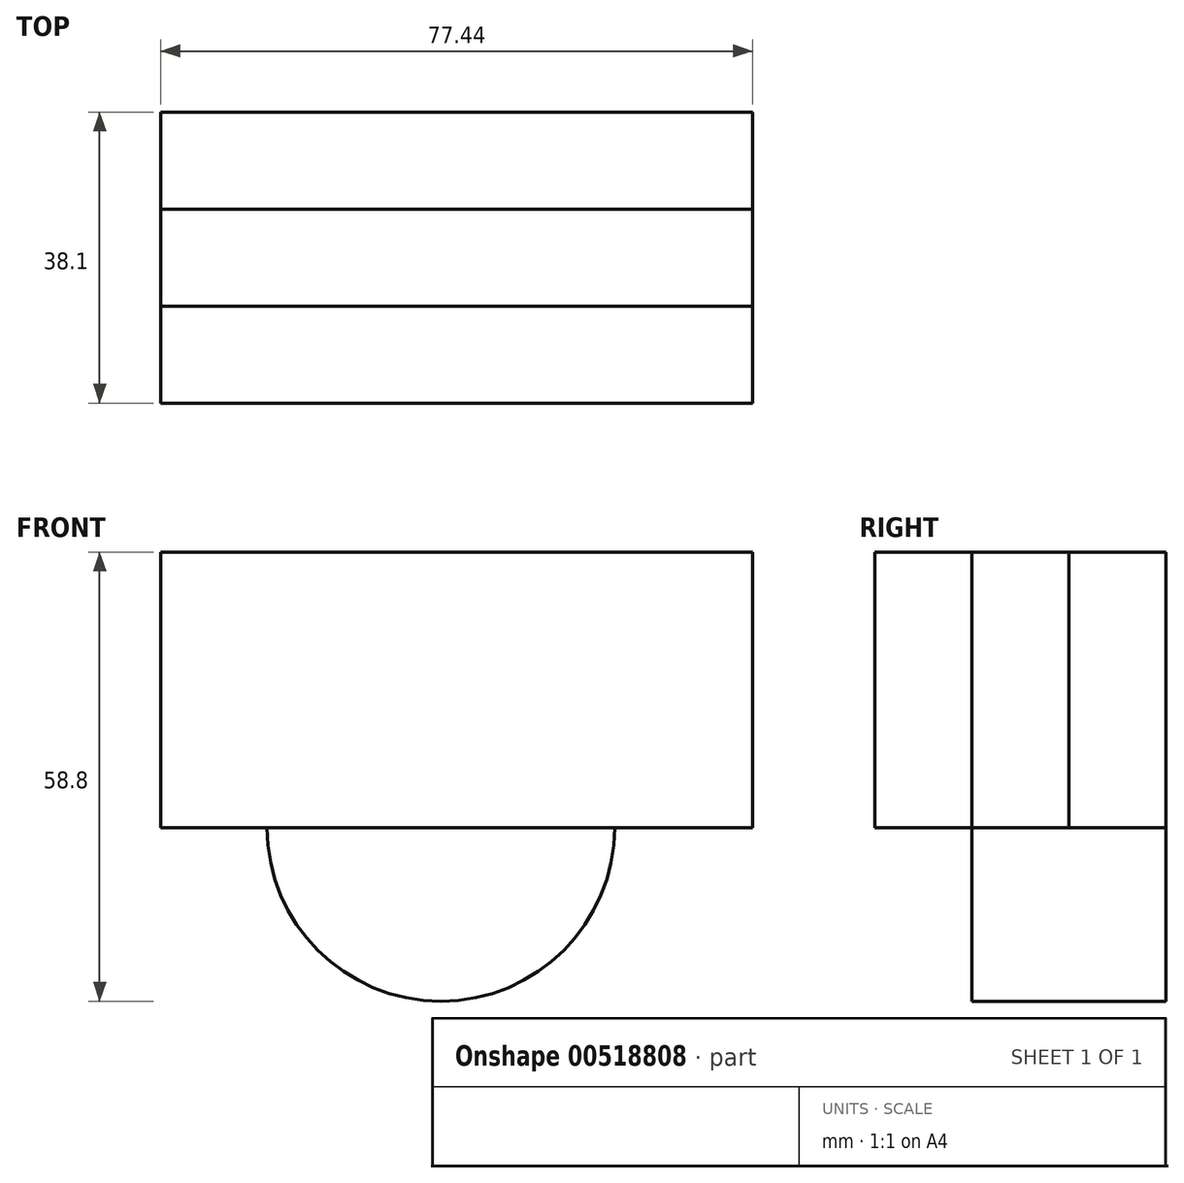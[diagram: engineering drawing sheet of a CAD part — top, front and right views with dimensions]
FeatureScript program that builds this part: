
annotation { "Feature Type Name" : "Feature", "Feature Type Description" : "" }
export const myFeature = defineFeature(function(context is Context, id is Id, definition is map)
    precondition{}
    {
        {
            var Q0;
            Q0=qCreatedBy(makeId("Front.planeOp"),FACE);
            var sketch = newSketch(context, id + "F0", { "sketchPlane" : qUnion([Q0])});
            skLineSegment(sketch, "E0.bottom", {"start": v(-36.65, 36.06) * mm, "end": v(40.8, 36.06) * mm});
            skLineSegment(sketch, "E0.top", {"start": v(-36.65, 0) * mm, "end": v(40.8, 0) * mm});
            skLineSegment(sketch, "E0.left", {"start": v(-36.65, 36.06) * mm, "end": v(-36.65, 0) * mm});
            skLineSegment(sketch, "E0.right", {"start": v(40.8, 36.06) * mm, "end": v(40.8, 0) * mm});
            skSolve(sketch);
        }
        {
            var Q0;
            Q0 = qSketchRegion(id + "F0", true);
            extrude(context, id + "F1", {"entities" : qUnion([Q0]), "depth" : 25.4 * mm});
        }
        {
            var Q0;
            Q0=makeQuery(id+"F1.opExtrude","CAP_FACE",FACE,{"disambiguationData":[OSD([sQuery(id+"F0.wireOp",EDGE,"E0.bottom"),sQuery(id+"F0.wireOp",EDGE,"E0.top"),sQuery(id+"F0.wireOp",EDGE,"E0.left"),sQuery(id+"F0.wireOp",EDGE,"E0.right")])],"isStart":true});
            var sketch = newSketch(context, id + "F2", { "sketchPlane" : qUnion([Q0])});
            skCircle(sketch, "E1", {"center": v(0, 0) * mm, "radius": 22.74 * mm});
            skSolve(sketch);
        }
        {
            var Q0;
            Q0=makeQuery(id+"F2.imprint","IMPRINT",FACE,{"disambiguationData":[TD([[makeQuery(id+"F2.imprint","IMPRINT",EDGE,{"derivedFrom":makeQuery(id+"F1.opExtrude","CAP_EDGE",EDGE,{"disambiguationData":[OSD([sQuery(id+"F0.wireOp",EDGE,"E0.bottom")])],"isStart":true})}),1.0]])]});
            var Q1;
            {var subQ0=sQuery(id+"F2.wireOp",EDGE,"E1");var subQ1=makeQuery(id+"F1.opExtrude","CAP_EDGE",EDGE,{"disambiguationData":[OSD([sQuery(id+"F0.wireOp",EDGE,"E0.top")])],"isStart":true});var subQ2=makeQuery(id+"F2.imprint","INTERSECT",VERTEX,{"disambiguationData":[OD(0.0)],"derivedFrom":[subQ1,subQ0]});Q1=makeQuery(id+"F2.imprint","IMPRINT",FACE,{"disambiguationData":[TD([[makeQuery(id+"F2.imprint","IMPRINT",EDGE,{"disambiguationData":[TD([[subQ2,-1.0]])],"derivedFrom":subQ0}),1.0]])]});}
            var Q2;
            {var subQ0=sQuery(id+"F2.wireOp",EDGE,"E1");var subQ1=makeQuery(id+"F1.opExtrude","CAP_EDGE",EDGE,{"disambiguationData":[OSD([sQuery(id+"F0.wireOp",EDGE,"E0.top")])],"isStart":true});var subQ2=makeQuery(id+"F2.imprint","INTERSECT",VERTEX,{"disambiguationData":[OD(0.0)],"derivedFrom":[subQ1,subQ0]});Q2=makeQuery(id+"F2.imprint","IMPRINT",FACE,{"disambiguationData":[TD([[makeQuery(id+"F2.imprint","IMPRINT",EDGE,{"disambiguationData":[TD([[subQ2,1.0]])],"derivedFrom":subQ0}),1.0]])]});}
            extrude(context, id + "F3", {"entities" : qUnion([Q0, Q1, Q2]), "endBound" : BoundingType.SYMMETRIC, "oppositeDirection" : true, "depth" : 25.4 * mm});
        }
    });
